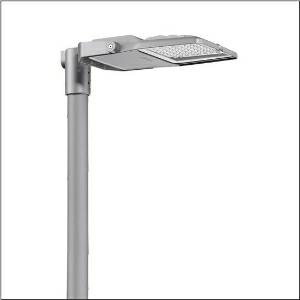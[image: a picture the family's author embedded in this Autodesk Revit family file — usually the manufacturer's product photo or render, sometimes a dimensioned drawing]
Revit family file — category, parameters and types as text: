
# Revit family: floodlight_fl_21_iq_mini___pl43_5xa7771b4a3a_ae81
name_source: partatom
category: Lighting Fixtures
units: mm (PartAtom-declared; Revit-internal decimal feet)

## family parameters
Cut with Voids When Loaded = No
Host = Face
Light Source = No
Part Type = Normal
Room Calculation Point = No
Round Connector Dimension = Use Diameter
Shared = No

## types (1)
- --- (1 x LED, 6660 lm, 45.5 W, 4000K)
    Apparent Load = 46 VA
    CIE Flux Codes = 27 78 99 100 100
    Color Rendering = 70
    Color Temperature = 4000K
    Default Elevation = 1800 mm
    Description = Floodlight FL 21 iQ mini, floodlight, primary light control with lens, of PMMA, primary optical cover: protective disc, of toughened safety glass, transparent, light distribution: PL43, light emission: direct distribution, installation type: surface-mounted, LED, High Power LED, rated luminous flux: 6.660lm, luminous efficacy: 146lm/W, light colour: 740, colour temperature: 4000K, control gear: iQ Comfort/DALI, control: Auto-Match, Temp-Guard, Lumen-Switch, Night-Set, Smart-Wire, Light-Fading, Desk-Remote (wireless, voltage-free reading and setting of iQ features in the workshop via application-optimized NFC function/RFID function), optimised constant luminous flux control (CLO 2.0), with terminal, 6-pole, mains connection: 220..240V, AC, 50/60Hz, start of lifetime: 46W, end of service life: 48W, reduction: 22W, luminaire housing, of diecast aluminium, powder-coated, Siteco® metallic grey (DB 702S), corrosivity category C5 mid according to DIN EN ISO 12944, suitable for swimming pools, chlorine-resistant, sealing non-destructively replaceable, please order mast flange separately, mast bracket, of steel, galvanised, powder-coated, Siteco® metallic grey (DB 702S), protection rating (complete): IP66, insulation class (complete): insulation class II (safety insulation), certification: CE, ENEC, VDE, protection symbol: D, impact resistance: IK08, permissible operating ambient temperature: -40..+40°C, permissible operating ambient temperature for outdoor applications: -40..+50°C, standard: DIN EN 12944, LABS conformity tested according to VDMA 24364:2018-05, packaging unit: 1 piece

Light Distribution: PL43
    Height = 70 mm
    Lamp = 1 x LED
    Lamp Light Flux = 6660 lm
    Lamp Power = 45.5 W
    Lamp count = 1
    Length = 485 mm
    Luminous efficacy = 146 lm/W
    Manufacturer = Siteco
    ModVariant = No
    Model = 5XA7771B4A3A
    Number of Poles = 1
    OnlyDefault = Yes
    Power Factor = 1
    Product Name = Floodlight FL 21 iQ mini | PL43
    Product group = floodlight | pylon annexe
    ProductGroupID = 6201
    Protection Class = Protection class II
    Protection Degree = IP 66
    RLX_Detail_Level = 1
    RLX_Emergency_Light_Flux = 0 lm
    RLX_Emergency_Type = 0
    RLX_Emergency_Type_DB = No
    RlxData = <blob elided: 101209 chars, md5=e28c5da8>
    Socket = socket
    Standby Power = 0 W
    System Light Flux = 6660 lm
    System Power = 46 W
    Type Comments = factory setting: luminous flux: 100 % | dim-lin: 254 | 463 mA
    Type Image = l_1007125.jpg
    URL = http://relux.com
    VarID = @adj_184347
    Voltage = 0 V
    Weight = 0.00 kg
    Width = 337 mm

## geometry (parser evidence)
native form markers: Blend x4, Sweep x14
no freeform markers — native parametric forms only
